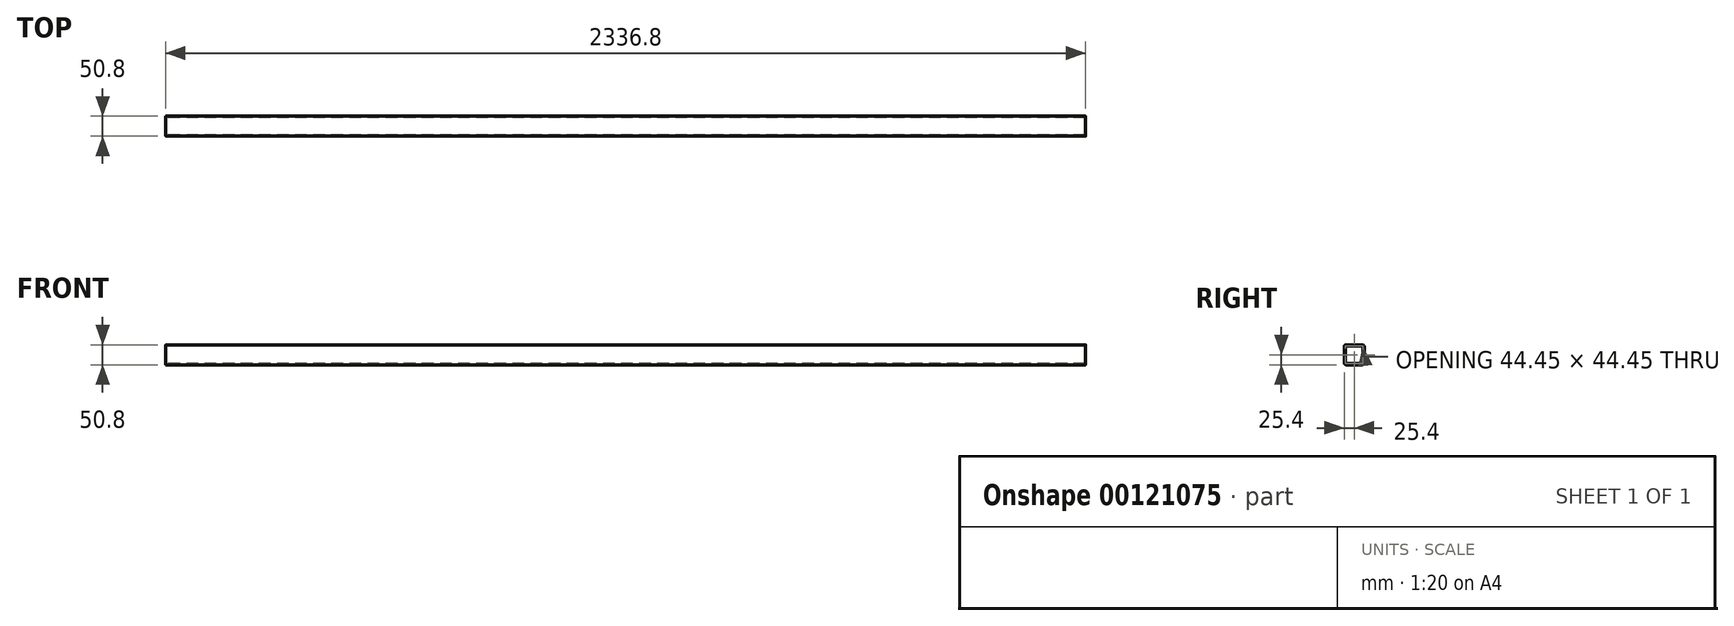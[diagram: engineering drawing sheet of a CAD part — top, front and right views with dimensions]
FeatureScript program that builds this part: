
annotation { "Feature Type Name" : "Feature", "Feature Type Description" : "" }
export const myFeature = defineFeature(function(context is Context, id is Id, definition is map)
    precondition{}
    {
        {
            var Q0;
            Q0=qCreatedBy(makeId("Right.planeOp"),FACE);
            var sketch = newSketch(context, id + "F0", { "sketchPlane" : qUnion([Q0])});
            skLineSegment(sketch, "E0.bottom", {"start": v(25.4, 25.4) * mm, "end": v(-25.4, 25.4) * mm});
            skLineSegment(sketch, "E0.top", {"start": v(25.4, -25.4) * mm, "end": v(-25.4, -25.4) * mm});
            skLineSegment(sketch, "E0.left", {"start": v(25.4, 25.4) * mm, "end": v(25.4, -25.4) * mm});
            skLineSegment(sketch, "E0.right", {"start": v(-25.4, 25.4) * mm, "end": v(-25.4, -25.4) * mm});
            skPoint(sketch, "E0.middle", {"position": v(0, 0) * mm});
            skSolve(sketch);
        }
        {
            var Q0;
            Q0 = qSketchRegion(id + "F0", true);
            var Q1;
            Q1=sQuery(id+"F0.wireOp",EDGE,"E0.right");
            var Q2;
            Q2=sQuery(id+"F0.wireOp",EDGE,"E0.bottom");
            var Q3;
            Q3=sQuery(id+"F0.wireOp",EDGE,"E0.left");
            var Q4;
            Q4=sQuery(id+"F0.wireOp",EDGE,"E0.top");
            extrude(context, id + "F1", {"entities" : qUnion([Q0]), "surfaceEntities" : qUnion([Q1, Q2, Q3, Q4]), "endBound" : BoundingType.SYMMETRIC, "depth" : 2336.8 * mm});
        }
        {
            var Q0;
            Q0=makeQuery(id+"F1.opExtrude","CAP_FACE",FACE,{"disambiguationData":[OSD([sQuery(id+"F0.wireOp",EDGE,"E0.bottom"),sQuery(id+"F0.wireOp",EDGE,"E0.top"),sQuery(id+"F0.wireOp",EDGE,"E0.left"),sQuery(id+"F0.wireOp",EDGE,"E0.right")])],"isStart":false});
            var Q1;
            Q1=makeQuery(id+"F1.opExtrude","CAP_FACE",FACE,{"disambiguationData":[OSD([sQuery(id+"F0.wireOp",EDGE,"E0.bottom"),sQuery(id+"F0.wireOp",EDGE,"E0.top"),sQuery(id+"F0.wireOp",EDGE,"E0.left"),sQuery(id+"F0.wireOp",EDGE,"E0.right")])],"isStart":true});
            shell(context, id + "F2", {"entities" : qUnion([Q0, Q1]), "thickness" : 3.17 * mm});
        }
        {
            var Q0;
            Q0=makeQuery(id+"F1.opExtrude","SWEPT_EDGE",EDGE,{"disambiguationData":[OSD([sQuery(id+"F0.wireOp",EDGE,"E0.bottom"),sQuery(id+"F0.wireOp",EDGE,"E0.left")])]});
            var Q1;
            Q1=makeQuery(id+"F1.opExtrude","SWEPT_EDGE",EDGE,{"disambiguationData":[OSD([sQuery(id+"F0.wireOp",EDGE,"E0.bottom"),sQuery(id+"F0.wireOp",EDGE,"E0.right")])]});
            var Q2;
            Q2=makeQuery(id+"F1.opExtrude","SWEPT_EDGE",EDGE,{"disambiguationData":[OSD([sQuery(id+"F0.wireOp",EDGE,"E0.top"),sQuery(id+"F0.wireOp",EDGE,"E0.left")])]});
            var Q3;
            Q3=makeQuery(id+"F1.opExtrude","SWEPT_EDGE",EDGE,{"disambiguationData":[OSD([sQuery(id+"F0.wireOp",EDGE,"E0.top"),sQuery(id+"F0.wireOp",EDGE,"E0.right")])]});
            fillet(context, id + "F3", {"entities" : qUnion([Q0, Q1, Q2, Q3]), "radius" : 4.76 * mm, "tangentPropagation" : true, "allowEdgeOverflow" : false});
        }
        {
            var Q0;
            Q0=makeQuery(id+"F2.opShell","OFFSET_EDGE",EDGE,{"disambiguationData":[OSD([sQuery(id+"F0.wireOp",EDGE,"E0.bottom"),sQuery(id+"F0.wireOp",EDGE,"E0.right")])]});
            var Q1;
            Q1=makeQuery(id+"F2.opShell","OFFSET_EDGE",EDGE,{"disambiguationData":[OSD([sQuery(id+"F0.wireOp",EDGE,"E0.top"),sQuery(id+"F0.wireOp",EDGE,"E0.right")])]});
            var Q2;
            Q2=makeQuery(id+"F2.opShell","OFFSET_EDGE",EDGE,{"disambiguationData":[OSD([sQuery(id+"F0.wireOp",EDGE,"E0.top"),sQuery(id+"F0.wireOp",EDGE,"E0.left")])]});
            var Q3;
            Q3=makeQuery(id+"F2.opShell","OFFSET_EDGE",EDGE,{"disambiguationData":[OSD([sQuery(id+"F0.wireOp",EDGE,"E0.bottom"),sQuery(id+"F0.wireOp",EDGE,"E0.left")])]});
            fillet(context, id + "F4", {"entities" : qUnion([Q0, Q1, Q2, Q3]), "radius" : 2.38 * mm, "tangentPropagation" : true, "allowEdgeOverflow" : false});
        }
    });
